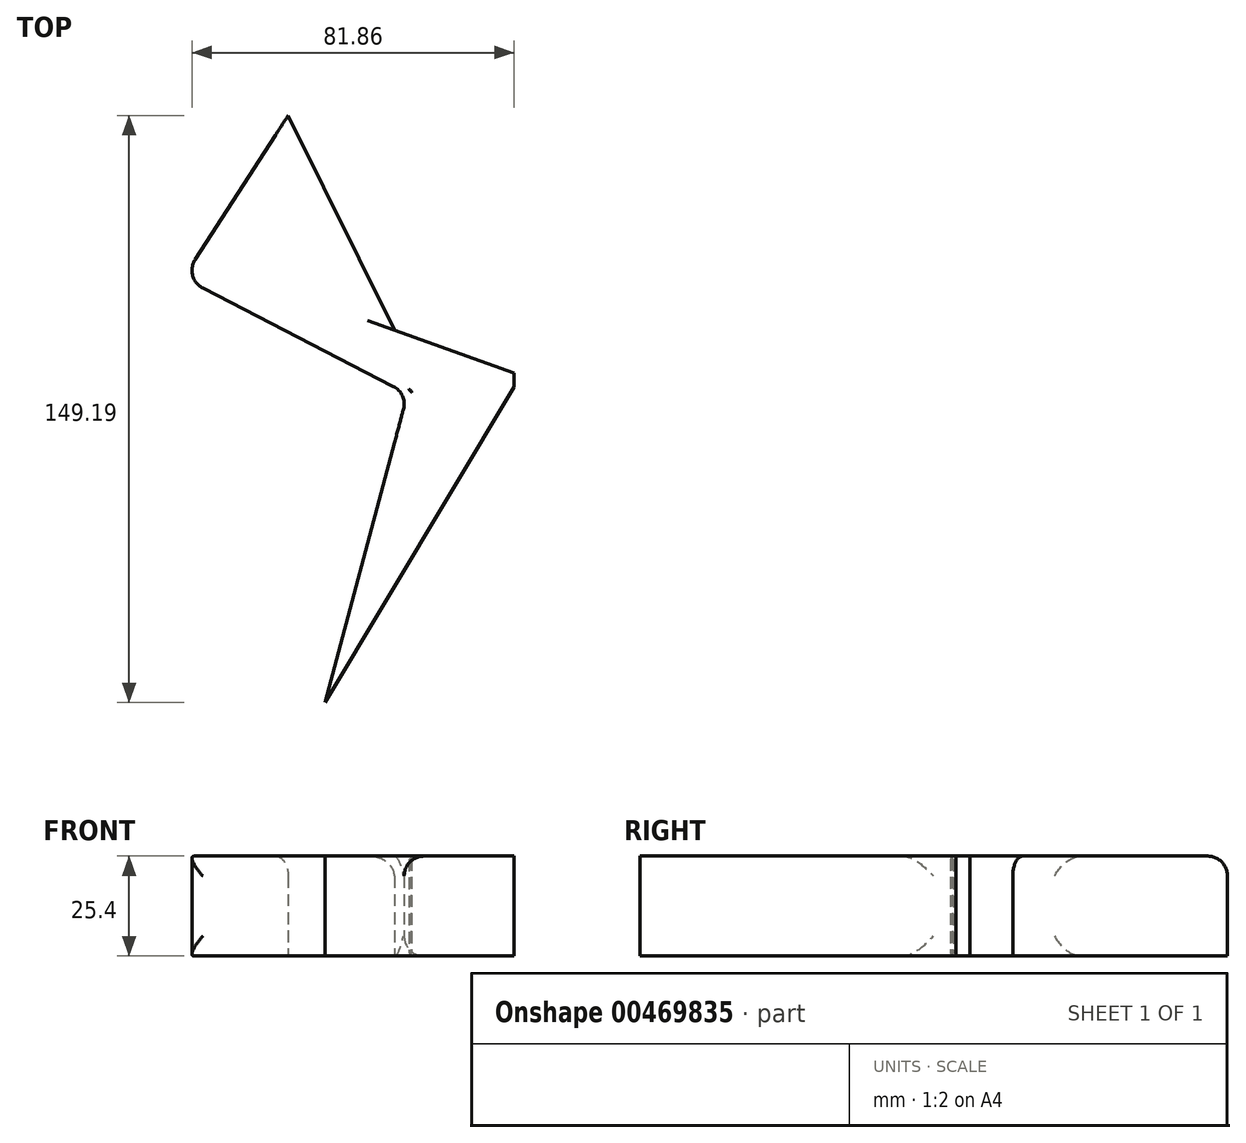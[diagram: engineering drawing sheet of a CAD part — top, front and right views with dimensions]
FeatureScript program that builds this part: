
annotation { "Feature Type Name" : "Feature", "Feature Type Description" : "" }
export const myFeature = defineFeature(function(context is Context, id is Id, definition is map)
    precondition{}
    {
        {
            var Q0;
            Q0=qCreatedBy(makeId("Top.planeOp"),FACE);
            var sketch = newSketch(context, id + "F0", { "sketchPlane" : qUnion([Q0])});
            skLineSegment(sketch, "E0", {"start": v(44.62, -38.34) * mm, "end": v(-12.53, -8.9) * mm});
            skLineSegment(sketch, "E1", {"start": v(-12.53, -8.9) * mm, "end": v(14.12, 32.44) * mm});
            skLineSegment(sketch, "E2", {"start": v(14.12, 32.44) * mm, "end": v(44.62, -29.16) * mm});
            skLineSegment(sketch, "E3", {"start": v(44.62, -29.16) * mm, "end": v(45.44, -37.94) * mm});
            skLineSegment(sketch, "E4", {"start": v(45.44, -37.94) * mm, "end": v(44.8, -37.12) * mm});
            skLineSegment(sketch, "E5", {"start": v(44.8, -37.12) * mm, "end": v(46.9, -38.33) * mm});
            skLineSegment(sketch, "E6", {"start": v(46.9, -38.33) * mm, "end": v(46.9, -39.66) * mm});
            skLineSegment(sketch, "E7", {"start": v(46.9, -39.66) * mm, "end": v(45.75, -43.29) * mm});
            skLineSegment(sketch, "E8", {"start": v(45.75, -43.29) * mm, "end": v(44.62, -38.34) * mm});
            skLineSegment(sketch, "E9", {"start": v(44.52, -38) * mm, "end": v(23.53, -116.75) * mm});
            skLineSegment(sketch, "E10", {"start": v(23.53, -116.75) * mm, "end": v(71.55, -36.58) * mm});
            skLineSegment(sketch, "E11", {"start": v(71.55, -36.58) * mm, "end": v(71.55, -32.97) * mm});
            skLineSegment(sketch, "E12", {"start": v(71.55, -32.97) * mm, "end": v(41.12, -22.09) * mm});
            skSolve(sketch);
        }
        {
            var Q0;
            {var subQ5=sQuery(id+"F0.wireOp",EDGE,"E6");Q0=makeQuery(id+"F0.imprint","IMPRINT",FACE,{"disambiguationData":[TD([[makeQuery(id+"F0.imprint","IMPRINT",EDGE,{"derivedFrom":subQ5}),1.0]])]});}
            var Q1;
            {var subQ11=sQuery(id+"F0.wireOp",EDGE,"E1");Q1=makeQuery(id+"F0.imprint","IMPRINT",FACE,{"disambiguationData":[TD([[makeQuery(id+"F0.imprint","IMPRINT",EDGE,{"derivedFrom":subQ11}),-1.0]])]});}
            extrude(context, id + "F1", {"entities" : qUnion([Q0, Q1]), "depth" : 25.4 * mm});
        }
        {
            var Q0;
            Q0=makeQuery(id+"F1.opExtrude","CAP_EDGE",EDGE,{"disambiguationData":[OSD([sQuery(id+"F0.wireOp",EDGE,"E2")])],"isStart":false});
            fillet(context, id + "F2", {"entities" : qUnion([Q0]), "radius" : 5.08 * mm, "tangentPropagation" : true, "allowEdgeOverflow" : false});
        }
        {
            var Q0;
            Q0=makeQuery(id+"F1.opExtrude","SWEPT_FACE",FACE,{"disambiguationData":[OSD([sQuery(id+"F0.wireOp",EDGE,"E0")])]});
            fillet(context, id + "F3", {"entities" : qUnion([Q0]), "radius" : 5.08 * mm, "tangentPropagation" : true, "allowEdgeOverflow" : false});
        }
    });
